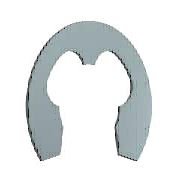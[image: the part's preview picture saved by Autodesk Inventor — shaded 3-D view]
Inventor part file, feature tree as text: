
AUTODESK INVENTOR PART (.ipt)
format: ipt  version: 2023.1 (Build 271208000, 208)  size: 156,672 bytes
history: native  units: mm (DEFAULTED — no unit token found)
features: other x2, plane x1
ambient origin geometry x8: Origin, YZ Plane, XZ Plane, XY Plane, X Axis, Y Axis, Z Axis, Center Point
bodies: Solid1 (feature_tree), Body (feature_tree)
feature tree (3):
  other  "Work Axis1"
  other  "Work Axis2"
  plane  "Work Plane1"
